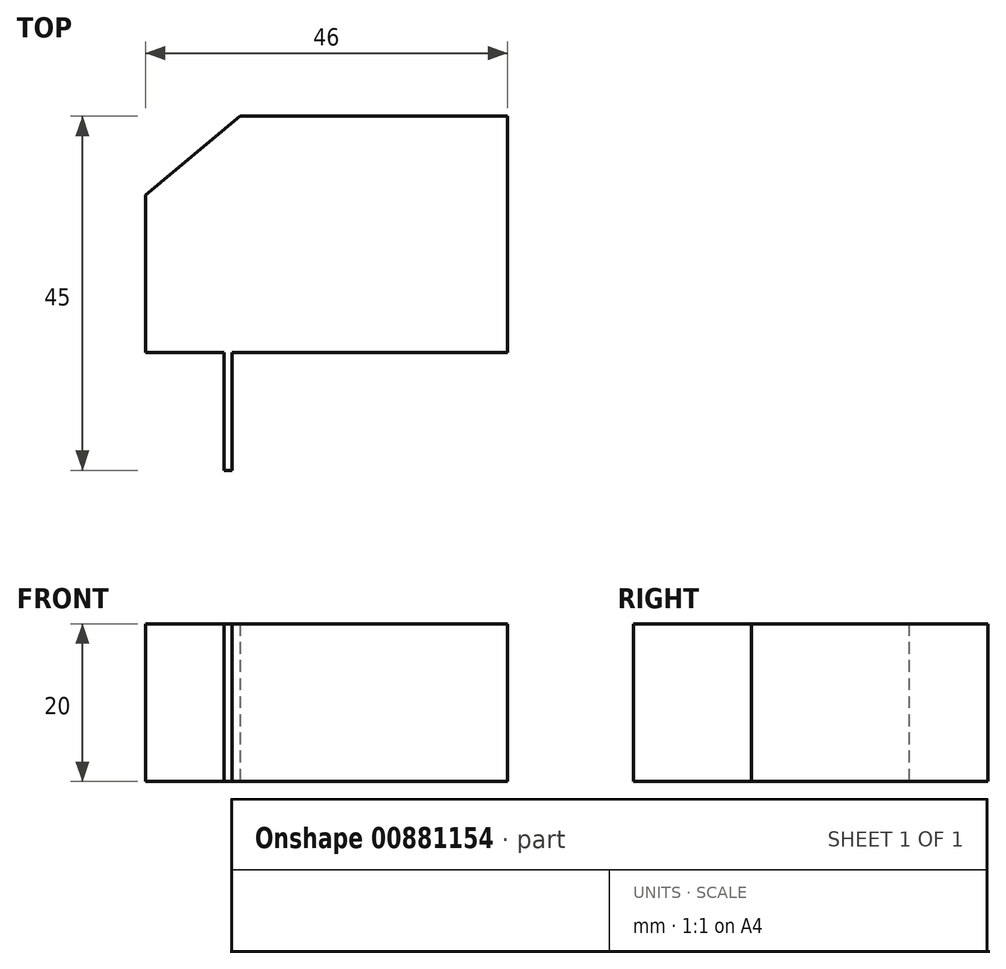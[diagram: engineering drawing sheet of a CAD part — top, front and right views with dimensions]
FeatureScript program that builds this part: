
annotation { "Feature Type Name" : "Feature", "Feature Type Description" : "" }
export const myFeature = defineFeature(function(context is Context, id is Id, definition is map)
    precondition{}
    {
        {
            var Q0;
            Q0=qCreatedBy(makeId("Top.planeOp"),FACE);
            var sketch = newSketch(context, id + "F0", { "sketchPlane" : qUnion([Q0])});
            skLineSegment(sketch, "E0.bottom", {"start": v(-2.71, 24.76) * mm, "end": v(31.29, 24.76) * mm});
            skLineSegment(sketch, "E0.top", {"start": v(-14.71, -5.24) * mm, "end": v(31.29, -5.24) * mm});
            skLineSegment(sketch, "E0.left", {"start": v(-14.71, 14.76) * mm, "end": v(-14.71, -5.24) * mm});
            skLineSegment(sketch, "E0.right", {"start": v(31.29, 24.76) * mm, "end": v(31.29, -5.24) * mm});
            skLineSegment(sketch, "E1", {"start": v(-14.71, 14.76) * mm, "end": v(-2.71, 24.76) * mm});
            skPoint(sketch, "E2.orphan", {"position": v(-14.71, 24.76) * mm});
            skLineSegment(sketch, "E3", {"start": v(-14.71, -5.24) * mm, "end": v(-4.71, -5.24) * mm, "construction": true});
            skLineSegment(sketch, "E4", {"start": v(-4.71, -5.24) * mm, "end": v(-4.71, -11.43) * mm, "construction": true});
            skLineSegment(sketch, "E5.bottom", {"start": v(-4.71, -5.24) * mm, "end": v(-3.71, -5.24) * mm});
            skLineSegment(sketch, "E5.top", {"start": v(-4.71, -20.24) * mm, "end": v(-3.71, -20.24) * mm});
            skLineSegment(sketch, "E5.left", {"start": v(-4.71, -5.24) * mm, "end": v(-4.71, -20.24) * mm});
            skLineSegment(sketch, "E5.right", {"start": v(-3.71, -5.24) * mm, "end": v(-3.71, -20.24) * mm});
            skSolve(sketch);
        }
        {
            var Q0;
            Q0=makeQuery(id+"F0.imprint","IMPRINT",FACE,{"disambiguationData":[TD([[makeQuery(id+"F0.imprint","IMPRINT",EDGE,{"derivedFrom":sQuery(id+"F0.wireOp",EDGE,"E0.bottom")}),-1.0]])]});
            var Q1;
            Q1=makeQuery(id+"F0.imprint","IMPRINT",FACE,{"disambiguationData":[TD([[makeQuery(id+"F0.imprint","IMPRINT",EDGE,{"derivedFrom":sQuery(id+"F0.wireOp",EDGE,"E5.top")}),1.0]])]});
            extrude(context, id + "F1", {"entities" : qUnion([Q0, Q1]), "depth" : 20 * mm, "offsetDistance" : 25 * mm});
        }
    });
